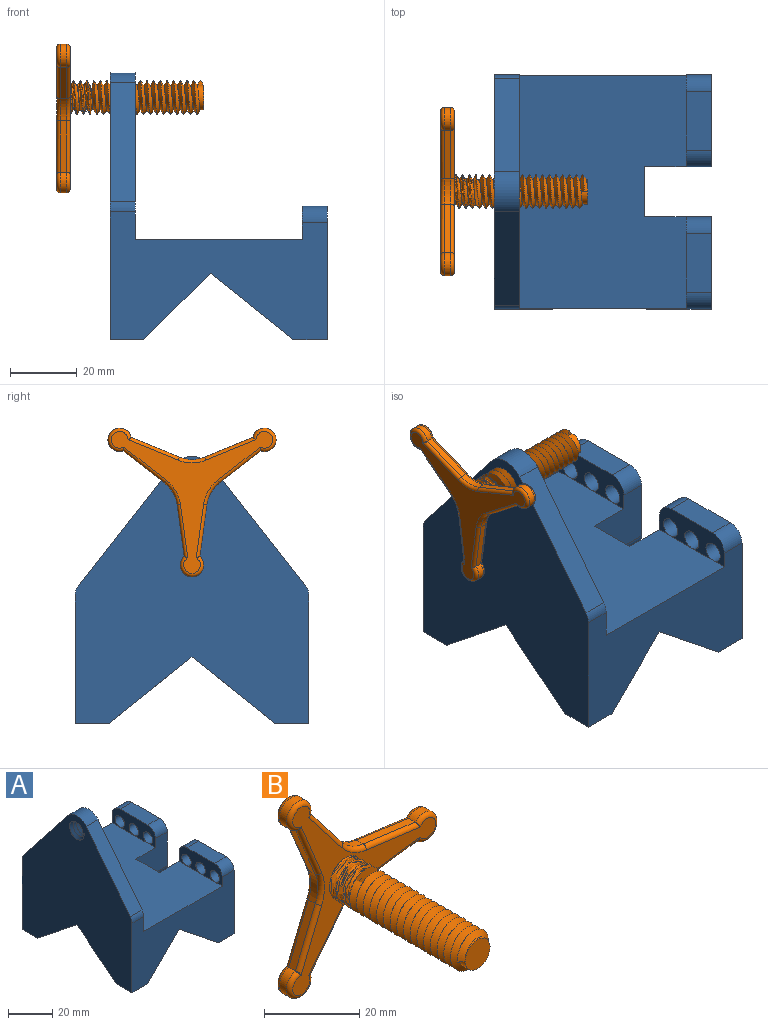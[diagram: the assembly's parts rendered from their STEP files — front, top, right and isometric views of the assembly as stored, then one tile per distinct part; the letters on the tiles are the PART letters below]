
ASSEMBLY  parts=2 mates=1
PART A: 47 faces, bbox 66.5x70.4x80.4 mm
  f0: plane 80.38x70.38mm, normal (-1,0,0), area 3776.5mm2, adj f1,f2,f3,f4,f5,f7,f22,f23
  f1: plane 10x10mm, normal (0,0,-1), area 100mm2, adj f0,f3,f7,f27
  f2: plane 10x10mm, normal (0,0,-1), area 100mm2, adj f0,f4,f5,f28
  f3: plane 65x38.27mm, normal (0,-1,0), area 1599.6mm2, adj f0,f1,f10,f11,f15,f18,f19,f26
  f4: plane 65x38.27mm, normal (0,1,0), area 1599.6mm2, adj f0,f2,f9,f15,f17,f19,f21,f28
  f5: plane 30x25mm, normal (0,-0.62,-0.78), area 640.3mm2, adj f0,f2,f7,f28
  f6: plane 35x25mm, normal (0,-0.62,-0.78), area 480.2mm2, adj f8,f9,f14,f17,f29,f37
  f7: plane 30x25mm, normal (0,0.62,-0.78), area 640.3mm2, adj f0,f1,f5,f27
  f8: plane 35x25mm, normal (0,0.62,-0.78), area 480.2mm2, adj f6,f10,f11,f14,f26,f36
  f9: plane 40x27.5mm, normal (1,0,0), area 881.1mm2, adj f4,f6,f13,f17,f20,f30,f31,f32
  f10: plane 40x27.5mm, normal (1,0,0), area 881.1mm2, adj f3,f8,f11,f12,f16,f33,f34,f35
  f11: plane 10x10mm, normal (0,0,-1), area 100mm2, adj f3,f8,f10,f26
  f12: plane 20x18.6mm, normal (0,1,0), area 309.4mm2, adj f10,f14,f18,f19,f36,f41
  f13: plane 20x18.6mm, normal (0,-1,0), area 309.4mm2, adj f9,f14,f19,f21,f37,f40
  f14: plane 18.75x17.5mm, normal (1,0,0), area 196.6mm2, adj f6,f8,f12,f13,f19,f36,f37
  f15: plane 70x50mm, normal (1,0,0), area 2174.2mm2, adj f3,f4,f19,f22,f23,f24,f25,f38
  f16: plane 17.5x7.5mm, normal (0,0,1), area 131.2mm2, adj f10,f18,f41,f43
  f17: plane 10x10mm, normal (0,0,-1), area 100mm2, adj f4,f6,f9,f29
  f18: plane 27.5x10mm, normal (-1,0,0), area 179.4mm2, adj f3,f12,f16,f19,f33,f34,f35,f41
  f19: plane 70x50mm, normal (0,0,1), area 3312.5mm2, adj f3,f4,f12,f13,f14,f15,f18,f21
  f20: plane 17.5x7.5mm, normal (0,0,1), area 131.2mm2, adj f9,f21,f40,f42
  f21: plane 27.5x10mm, normal (-1,0,0), area 179.4mm2, adj f4,f13,f19,f20,f30,f31,f32,f40
  f22: cylinder r=3.75mm len=7.5mm, axis (1,0,0), area 4.2mm2, adj f0,f15,f44,f45,f46
  f23: cylinder r=7.5mm len=11.81mm, axis (1,0,0), area 101.9mm2, adj f0,f15,f24,f25
  f24: plane 35.77x28.03mm, normal (0,0.79,0.62), area 340.8mm2, adj f0,f15,f23,f39
  f25: plane 35.77x28.03mm, normal (0,-0.79,0.62), area 340.8mm2, adj f0,f15,f23,f38
  f26: plane 35x25mm, normal (-0.62,0,-0.78), area 720.4mm2, adj f3,f8,f11,f27
  f27: plane 35x20mm, normal (0.71,0,-0.71), area 636.4mm2, adj f1,f3,f7,f26
  f28: plane 35x20mm, normal (0.71,0,-0.71), area 636.4mm2, adj f2,f4,f5,f29
  f29: plane 35x25mm, normal (-0.62,0,-0.78), area 720.4mm2, adj f4,f6,f17,f28
  f30: cylinder r=3mm len=7.5mm, axis (1,0,0), area 141.4mm2, adj f9,f21
  f31: cylinder r=3mm len=7.5mm, axis (1,0,0), area 141.4mm2, adj f9,f21
  f32: cylinder r=3mm len=7.5mm, axis (1,0,0), area 141.4mm2, adj f9,f21
  f33: cylinder r=3mm len=7.5mm, axis (1,0,0), area 141.4mm2, adj f10,f18
  f34: cylinder r=3mm len=7.5mm, axis (1,0,0), area 141.4mm2, adj f10,f18
  f35: cylinder r=3mm len=7.5mm, axis (1,0,0), area 141.4mm2, adj f10,f18
  f36: cylinder r=5mm len=20mm, axis (-1,0,0), area 89.6mm2, adj f8,f10,f12,f14
  f37: cylinder r=5mm len=20mm, axis (1,0,0), area 89.6mm2, adj f6,f9,f13,f14
  f38: cylinder r=5mm len=7.5mm, axis (-1,0,0), area 24.9mm2, adj f0,f3,f15,f25
  f39: cylinder r=5mm len=7.5mm, axis (-1,0,0), area 24.9mm2, adj f0,f4,f15,f24
  f40: cylinder r=5mm len=7.5mm, axis (1,0,0), area 58.9mm2, adj f9,f13,f20,f21
  f41: cylinder r=5mm len=7.5mm, axis (-1,0,0), area 58.9mm2, adj f10,f12,f16,f18
  f42: cylinder r=5mm len=7.5mm, axis (-1,0,0), area 58.9mm2, adj f4,f9,f20,f21
  f43: cylinder r=5mm len=7.5mm, axis (1,0,0), area 58.9mm2, adj f3,f10,f16,f18
  f44: plane 0.81x0.45mm, normal (0,0,-1), area 0.2mm2, adj f0,f22,f46
  f45: bspline ~12.69x10.99mm, area 218.5mm2, adj f0,f15,f22,f46
  f46: bspline ~12.69x10.99mm, area 215.8mm2, adj f0,f15,f22,f44,f45
PART B: 43 faces, bbox 46.2x45.1x52 mm
  f0: bspline ~40.98x11.76mm, area 923.1mm2, adj f1,f2,f4,f5
  f1: bspline ~40.31x11.76mm, area 910mm2, adj f0,f2,f4,f5
  f2: cylinder r=3.7mm len=40mm, axis (0,1,0), area 277.9mm2, adj f0,f1,f3,f4,f5
  f3: plane 7.4x7.4mm, normal (0,-1,0), area 43mm2, adj f2
  f4: plane 1.95x1.39mm, normal (0,0,-1), area 1.4mm2, adj f0,f1,f2
  f5: plane 49.4x43.6mm, normal (0,-1,0), area 361.4mm2, adj f0,f1,f2,f19,f20,f21,f22,f23
  f6: plane 48.3x42.5mm, normal (0,1,0), area 422.1mm2, adj f31,f32,f33,f34,f35,f36,f37,f38
  f7: plane 12.34x9.55mm, normal (0.79,0,0.61), area 31.2mm2, adj f14,f16,f26,f38
  f8: plane 14.44x5.91mm, normal (-0.93,0,-0.38), area 31.2mm2, adj f14,f18,f30,f42
  f9: plane 14.44x5.91mm, normal (-0.93,0,0.38), area 31.2mm2, adj f15,f18,f27,f39
  f10: plane 12.34x9.55mm, normal (0.79,0,-0.61), area 31.2mm2, adj f15,f17,f23,f35
  f11: plane 15.46x2.1mm, normal (0.13,0,-0.99), area 31.2mm2, adj f13,f17,f19,f31
  f12: plane 15.46x2.1mm, normal (0.13,0,0.99), area 31.2mm2, adj f13,f16,f22,f34
  f13: cylinder r=3.5mm len=7mm, axis (0,1,0), area 33.7mm2, adj f11,f12,f20,f32
  f14: cylinder r=3.5mm len=7mm, axis (0,1,0), area 33.7mm2, adj f7,f8,f28,f40
  f15: cylinder r=3.5mm len=7mm, axis (0,1,0), area 33.7mm2, adj f9,f10,f25,f37
  f16: cylinder r=10mm len=6.57mm, axis (0,1,0), area 15.6mm2, adj f7,f12,f24,f36
  f17: cylinder r=10mm len=6.57mm, axis (0,1,0), area 15.6mm2, adj f10,f11,f21,f33
  f18: cylinder r=10mm len=7.58mm, axis (0,1,0), area 15.6mm2, adj f8,f9,f29,f41
  f19: cylinder r=1mm len=16.18mm, axis (0.99,0,0.13), area 25mm2, adj f5,f11,f20,f21
  f20: torus R=2.5mm, axis (0,1,0), area 24.6mm2, adj f5,f13,f19,f22
  f21: torus R=11mm, axis (0,1,0), area 12.7mm2, adj f5,f17,f19,f23
  f22: cylinder r=1mm len=16.18mm, axis (-0.99,0,0.13), area 25mm2, adj f5,f12,f20,f24
  f23: cylinder r=1mm len=13.42mm, axis (0.61,0,0.79), area 25mm2, adj f5,f10,f21,f25
  f24: torus R=11mm, axis (0,1,0), area 12.7mm2, adj f5,f16,f22,f26
  f25: torus R=2.5mm, axis (0,1,0), area 24.6mm2, adj f5,f15,f23,f27
  f26: cylinder r=1mm len=13.42mm, axis (-0.61,0,0.79), area 25mm2, adj f5,f7,f24,f28
  f27: cylinder r=1mm len=15.36mm, axis (-0.38,0,-0.93), area 25mm2, adj f5,f9,f25,f29
  f28: torus R=2.5mm, axis (0,1,0), area 24.6mm2, adj f5,f14,f26,f30
  f29: torus R=11mm, axis (0,1,0), area 12.7mm2, adj f5,f18,f27,f30
  f30: cylinder r=1mm len=15.36mm, axis (0.38,0,-0.93), area 25mm2, adj f5,f8,f28,f29
  f31: cylinder r=1mm len=16.18mm, axis (-0.99,0,-0.13), area 25mm2, adj f6,f11,f32,f33
  f32: torus R=2.5mm, axis (0,1,0), area 24.6mm2, adj f6,f13,f31,f34
  f33: torus R=11mm, axis (0,1,0), area 12.7mm2, adj f6,f17,f31,f35
  f34: cylinder r=1mm len=16.18mm, axis (0.99,0,-0.13), area 25mm2, adj f6,f12,f32,f36
  f35: cylinder r=1mm len=13.42mm, axis (-0.61,0,-0.79), area 25mm2, adj f6,f10,f33,f37
  f36: torus R=11mm, axis (0,1,0), area 12.7mm2, adj f6,f16,f34,f38
  f37: torus R=2.5mm, axis (0,1,0), area 24.6mm2, adj f6,f15,f35,f39
  f38: cylinder r=1mm len=13.42mm, axis (0.61,0,-0.79), area 25mm2, adj f6,f7,f36,f40
  f39: cylinder r=1mm len=15.36mm, axis (0.38,0,0.93), area 25mm2, adj f6,f9,f37,f41
  f40: torus R=2.5mm, axis (0,1,0), area 24.6mm2, adj f6,f14,f38,f42
  f41: torus R=11mm, axis (0,1,0), area 12.7mm2, adj f6,f18,f39,f42
  f42: cylinder r=1mm len=15.36mm, axis (-0.38,0,0.93), area 25mm2, adj f6,f8,f40,f41
PLACE A t=(-44.02,41.5,-19.84)mm fixed
PLACE B rot(axis=(-0.58,0.58,0.58),120deg) t=(-55.99,6.5,52.66)mm
MATE slider A.f23 <-> B.f2  axis (1,0,0) through (-36.52,6.5,52.66)mm
